# Revit family: BOX HB
name_source: partatom
category: Modelos genéricos
revit_build: Autodesk Revit 2017 (Build: 20160225_1515(x64)
units: mm (PartAtom-declared; Revit-internal decimal feet)

## family parameters
Compartido = No
Corte con vacíos al cargar = No
Cota de conector redondo = Diámetro de uso
Puede alojar armadura = No
Punto de cálculo de habitación = No
Se basa en plano de trabajo = No
Siempre vertical = Sí
Tipo de pieza = Normal

## types (5) — shared parameters
EspBoca = 2 mm  [stored 0.00656168 ft]
EspPeu = 3 mm  [stored 0.00984252 ft]
Fabricante = Casals Ventilación
H = 30 mm  [stored 0.0984252 ft]
URL = www.casals.com

## per-type parameters (varying)
| type | A | B | C | D | Dimensiones | F | J | O |
| BOX HB 45-50 | 651 mm  [stored 2.13583 ft] | 651 mm  [stored 2.13583 ft] | 467 mm  [stored 1.53215 ft] | 500 mm  [stored 1.64042 ft] | 651x711x570 | 500 mm  [stored 1.64042 ft] | 570 mm  [stored 1.87008 ft] | 60 mm  [stored 0.19685 ft] |
| BOX HB 56-63 | 782 mm | 782 mm | 542 mm  [stored 1.77822 ft] | 630 mm  [stored 2.06693 ft] | 781,5x841,5x665
781,5x841,5x665
781,5x841,5x665
781,5x841,5x665 | 630 mm  [stored 2.06693 ft] | 665 mm  [stored 2.18176 ft] | 60 mm  [stored 0.19685 ft] |
| BOX HB 71-80 | 952 mm | 952 mm | 597 mm  [stored 1.95866 ft] | 800 mm  [stored 2.62467 ft] | 951,5x1011,5x705 | 800 mm  [stored 2.62467 ft] | 705 mm  [stored 2.31299 ft] | 60 mm  [stored 0.19685 ft] |
| BOX HB 90-100 | 1177 mm | 1177 mm | 857 mm  [stored 2.81168 ft] | 1000 mm  [stored 3.28084 ft] | 1176,5x1266,5x965 | 1000 mm  [stored 3.28084 ft] | 965 mm  [stored 3.16601 ft] | 90 mm  [stored 0.295276 ft] |
| BOX HB 112-125 | 1417 mm | 1417 mm | 1019 mm  [stored 3.34318 ft] | 1250 mm  [stored 4.10105 ft] | 1416,5x1506,5x1125 | 1250 mm  [stored 4.10105 ft] | 1125 mm  [stored 3.69094 ft] | 90 mm  [stored 0.295276 ft] |

note: [stored X ft] marks values corroborated as IEEE doubles in the binary element streams (Revit-internal decimal feet)
